# Revit family: Economy_Cupboards
name_source: partatom
category: Furniture
revit_build: Autodesk Revit 2016 (Build: 20150714_1515(x64)
units: mm (PartAtom-declared; Revit-internal decimal feet)

## family parameters
Always vertical = Yes
Cut with Voids When Loaded = No
OmniClass Number = 23.40.20.00
OmniClass Title = General Furniture and Specialties
Room Calculation Point = No
Shared = No
Work Plane-Based = No

## types (3) — shared parameters
Depth = 400 mm  [stored 1.31234 ft]
Manufacturer = BISLEY
Model = Economy Cupboard
Width = 914 mm  [stored 2.99869 ft]
plinth height = 75 mm

## per-type parameters (varying)
| type | Height |
| E402A01 | 1000 mm  [stored 3.28084 ft] |
| E722A03 | 1806 mm  [stored 5.9252 ft] |
| E782A04 | 1950 mm  [stored 6.39764 ft] |

note: [stored X ft] marks values corroborated as IEEE doubles in the binary element streams (Revit-internal decimal feet)

## geometry (parser evidence)
native form markers: Sweep x2
no freeform markers — native parametric forms only
